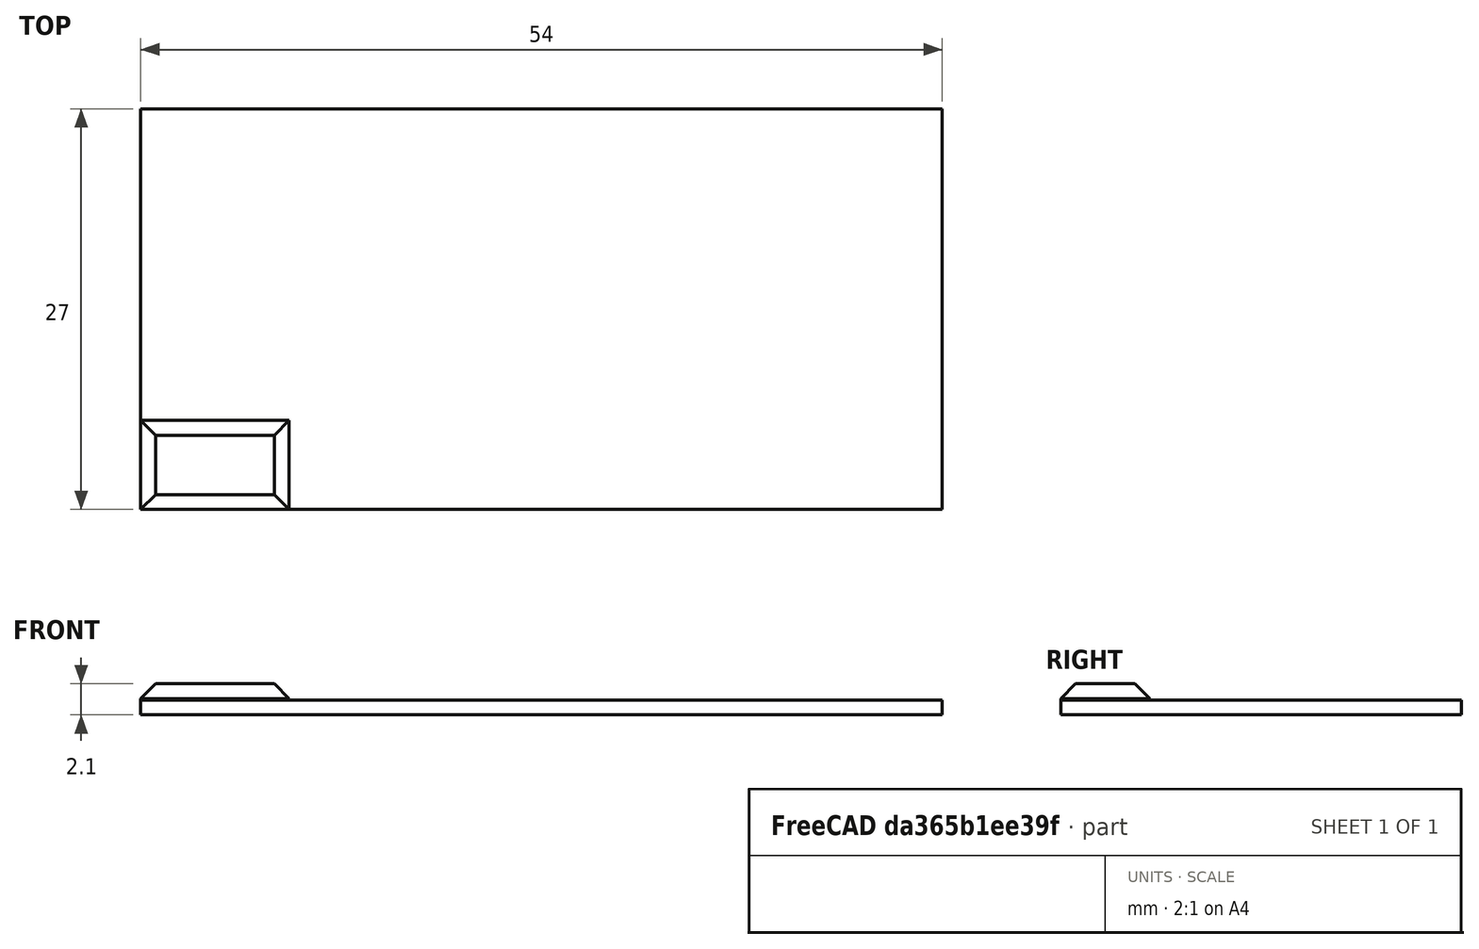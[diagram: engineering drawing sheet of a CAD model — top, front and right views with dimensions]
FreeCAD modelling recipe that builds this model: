
FCSTD DOCUMENT  (FreeCAD 0.21R33694 (Git))
Label: OJT1_T12P02.xocolata
License: All rights reserved
LicenseURL: http://en.wikipedia.org/wiki/All_rights_reserved
objects: Part::Box×2, Part::Chamfer×1, Part::FeaturePython×1
note: 3 computed .brp shape members not serialized (recipe doc carries the construction recipe); baked Part::Feature solids carry a one-line shape summary decoded from their .brp

FEATURE [Part::Box] Box  label="Cub"
  AttacherType = Attacher::AttachEngine3D
  Height = 1
  Length = 54
  Width = 27
FEATURE [Part::Box] Box001  label="Cub001"
  AttacherType = Attacher::AttachEngine3D
  Height = 1.1
  Length = 10
  Width = 6
FEATURE [Part::Chamfer] Chamfer
  Base = -> Box001
  Edges = 4 edges r=1: [Edge2,Edge6,Edge10,Edge12]
  Placement = pos=(0,0,1) rot=(0,0,1;0rad)
FEATURE [Part::FeaturePython] Array  # Draft array (typed FeaturePython)
  AlwaysSyncPlacement = false
  Angle = 360
  ArrayType = 0
  Axis = (0,0,1)
  Base = -> Chamfer
  Center = (0,0,0)
  Count = 20
  ExpandArray = false
  Fuse = false
  IntervalAxis = (0,0,0)
  IntervalX = (11,0,0)
  IntervalY = (0,7,0)
  IntervalZ = (0,0,100)
  NumberCircles = 3
  NumberPolar = 5
  NumberX = 5
  NumberY = 4
  NumberZ = 1
  PlacementList = 20 placements: [(0,0,1),(0,7,1),(0,14,1),(0,21,1),(11,0,1),(11,7,1),(11,14,1),(11,21,1),(22,0,1),(22,7,1),(22,14,1),(22,21,1),(33,0,1),(33,7,1),(33,14,1),(33,21,1),(44,0,1),(44,7,1),(44,14,1),(44,21,1)]
  RadialDistance = 50
  ScaleList = (20) [(1,1,1),(1,1,1),(1,1,1),(1,1,1),(1,1,1),(1,1,1),(1,1,1),(1,1,1),(1,1,1),(1,1,1),(1,1,1),(1,1,1),(1,1,1),(1,1,1),(1,1,1),(1,1,1),(1,1,1),(1,1,1),(1,1,1),(1,1,1)]
  Symmetry = 1
  TangentialDistance = 25
